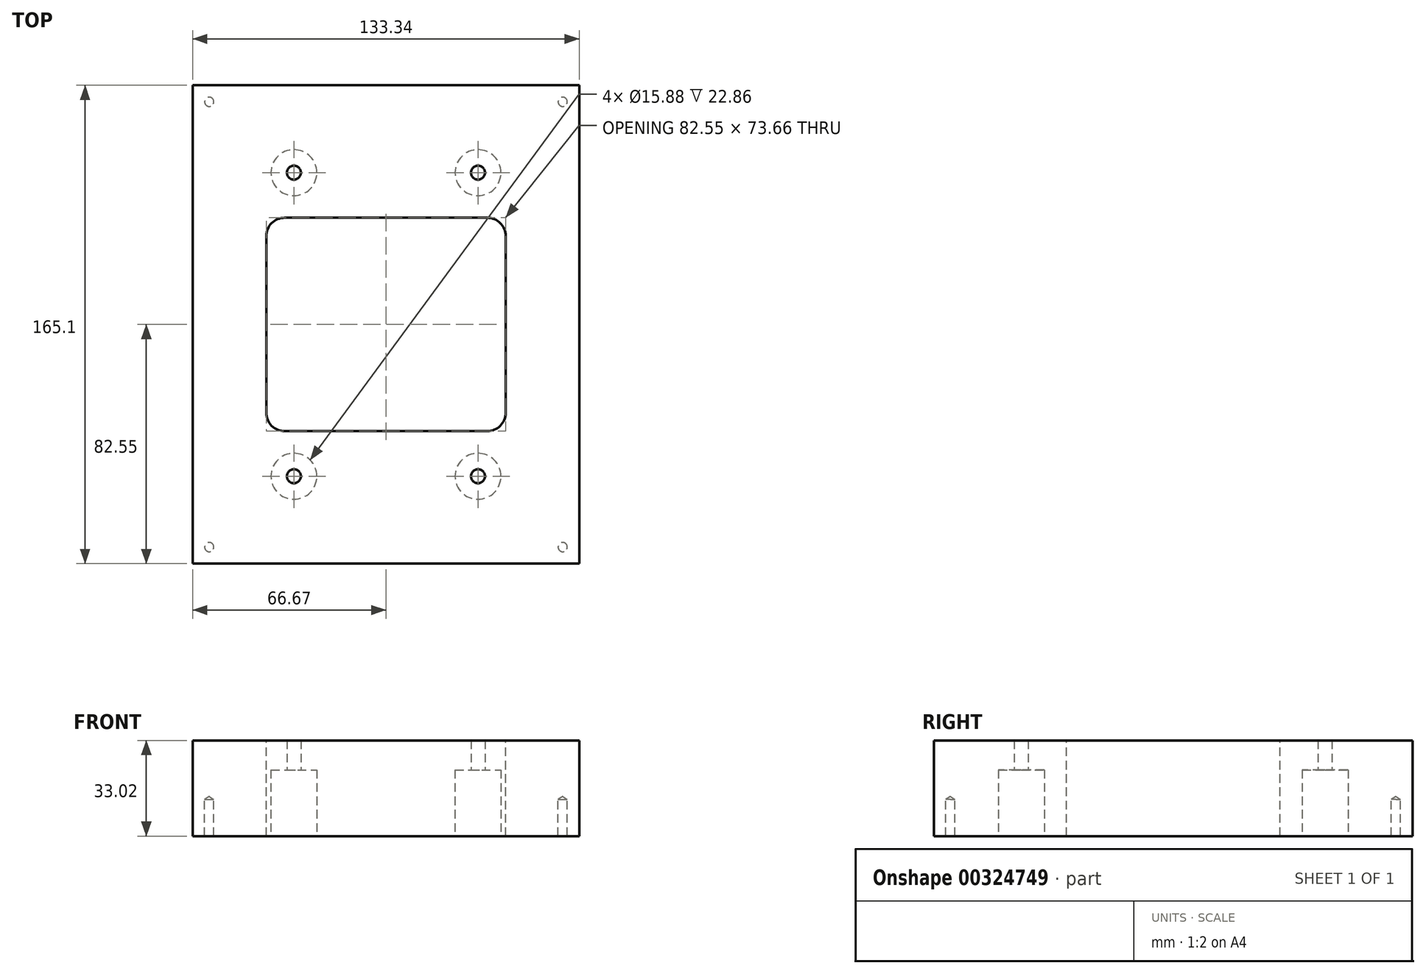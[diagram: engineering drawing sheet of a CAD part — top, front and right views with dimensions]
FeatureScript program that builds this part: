
annotation { "Feature Type Name" : "Feature", "Feature Type Description" : "" }
export const myFeature = defineFeature(function(context is Context, id is Id, definition is map)
    precondition{}
    {
        {
            var Q0;
            Q0=qCreatedBy(makeId("Top.planeOp"),FACE);
            var sketch = newSketch(context, id + "F0", { "sketchPlane" : qUnion([Q0])});
            skLineSegment(sketch, "E0.bottom", {"start": v(66.68, -82.55) * mm, "end": v(-66.68, -82.55) * mm});
            skLineSegment(sketch, "E0.top", {"start": v(66.68, 82.55) * mm, "end": v(-66.67, 82.55) * mm});
            skLineSegment(sketch, "E0.left", {"start": v(66.68, -82.55) * mm, "end": v(66.68, 82.55) * mm});
            skLineSegment(sketch, "E0.right", {"start": v(-66.68, -82.55) * mm, "end": v(-66.67, 82.55) * mm});
            skPoint(sketch, "E0.middle", {"position": v(0, 0) * mm});
            skSolve(sketch);
        }
        {
            var Q0;
            Q0 = qSketchRegion(id + "F0", true);
            extrude(context, id + "F1", {"entities" : qUnion([Q0]), "depth" : 33.02 * mm, "offsetDistance" : 25.4 * mm});
        }
        {
            var Q0;
            Q0=makeQuery(id+"F1.opExtrude","CAP_FACE",FACE,{"disambiguationData":[OSD([sQuery(id+"F0.wireOp",EDGE,"E0.bottom"),sQuery(id+"F0.wireOp",EDGE,"E0.top"),sQuery(id+"F0.wireOp",EDGE,"E0.left"),sQuery(id+"F0.wireOp",EDGE,"E0.right")])],"isStart":false});
            var sketch = newSketch(context, id + "F2", { "sketchPlane" : qUnion([Q0])});
            skLineSegment(sketch, "E1.bottom", {"start": v(-41.28, 36.83) * mm, "end": v(41.28, 36.83) * mm});
            skLineSegment(sketch, "E1.top", {"start": v(-41.28, -36.83) * mm, "end": v(41.28, -36.83) * mm});
            skLineSegment(sketch, "E1.left", {"start": v(-41.28, 36.83) * mm, "end": v(-41.28, -36.83) * mm});
            skLineSegment(sketch, "E1.right", {"start": v(41.28, 36.83) * mm, "end": v(41.28, -36.83) * mm});
            skSolve(sketch);
        }
        {
            var Q0;
            Q0=makeQuery(id+"F2.imprint","IMPRINT",FACE,{"disambiguationData":[TD([[makeQuery(id+"F2.imprint","IMPRINT",EDGE,{"derivedFrom":sQuery(id+"F2.wireOp",EDGE,"E1.bottom")}),-1.0]])]});
            extrude(context, id + "F3", {"entities" : qUnion([Q0]), "operationType" : NewBodyOperationType.REMOVE, "endBound" : BoundingType.THROUGH_ALL, "oppositeDirection" : true, "depth" : 25.4 * mm, "offsetDistance" : 25.4 * mm});
        }
        {
            var Q0;
            Q0=makeQuery(id+"F3.boolean.opBoolean","COPY",EDGE,{"derivedFrom":makeQuery(id+"F3.opExtrude","SWEPT_EDGE",EDGE,{"disambiguationData":[OSD([sQuery(id+"F2.wireOp",EDGE,"E1.bottom"),sQuery(id+"F2.wireOp",EDGE,"E1.left")])]})});
            var Q1;
            Q1=makeQuery(id+"F3.boolean.opBoolean","COPY",EDGE,{"derivedFrom":makeQuery(id+"F3.opExtrude","SWEPT_EDGE",EDGE,{"disambiguationData":[OSD([sQuery(id+"F2.wireOp",EDGE,"E1.top"),sQuery(id+"F2.wireOp",EDGE,"E1.left")])]})});
            var Q2;
            Q2=makeQuery(id+"F3.boolean.opBoolean","COPY",EDGE,{"derivedFrom":makeQuery(id+"F3.opExtrude","SWEPT_EDGE",EDGE,{"disambiguationData":[OSD([sQuery(id+"F2.wireOp",EDGE,"E1.top"),sQuery(id+"F2.wireOp",EDGE,"E1.right")])]})});
            var Q3;
            Q3=makeQuery(id+"F3.boolean.opBoolean","COPY",EDGE,{"derivedFrom":makeQuery(id+"F3.opExtrude","SWEPT_EDGE",EDGE,{"disambiguationData":[OSD([sQuery(id+"F2.wireOp",EDGE,"E1.bottom"),sQuery(id+"F2.wireOp",EDGE,"E1.right")])]})});
            fillet(context, id + "F4", {"entities" : qUnion([Q0, Q1, Q2, Q3]), "tangentPropagation" : true, "radius" : 6.35 * mm, "defaultsChanged" : false, "vertexSettings" : [], "allowEdgeOverflow" : false});
        }
        {
            var Q0;
            Q0=makeQuery(id+"F1.opExtrude","CAP_FACE",FACE,{"disambiguationData":[OSD([sQuery(id+"F0.wireOp",EDGE,"E0.bottom"),sQuery(id+"F0.wireOp",EDGE,"E0.top"),sQuery(id+"F0.wireOp",EDGE,"E0.left"),sQuery(id+"F0.wireOp",EDGE,"E0.right")])],"isStart":false});
            var sketch = newSketch(context, id + "F5", { "sketchPlane" : qUnion([Q0])});
            skPoint(sketch, "E2", {"position": v(-31.75, -52.39) * mm});
            skPoint(sketch, "E3", {"position": v(31.75, -52.39) * mm});
            skPoint(sketch, "E4", {"position": v(31.75, 52.39) * mm});
            skPoint(sketch, "E5", {"position": v(-31.75, 52.39) * mm});
            skSolve(sketch);
        }
        {
            var Q0;
            Q0=sQuery(id+"F5.wireOp",VERTEX,"E5");
            var Q1;
            Q1=sQuery(id+"F5.wireOp",VERTEX,"E4");
            var Q2;
            Q2=sQuery(id+"F5.wireOp",VERTEX,"E3");
            var Q3;
            Q3=sQuery(id+"F5.wireOp",VERTEX,"E2");
            var Q4;
            Q4=makeQuery(id+"F1.opExtrude","SWEPT_BODY",BODY,{"disambiguationData":[OSD([sQuery(id+"F0.wireOp",EDGE,"E0.bottom"),sQuery(id+"F0.wireOp",EDGE,"E0.top"),sQuery(id+"F0.wireOp",EDGE,"E0.left"),sQuery(id+"F0.wireOp",EDGE,"E0.right")])]});
            hole(context, id + "F6", {"style" : HoleStyle.SIMPLE, "endStyle" : HoleEndStyle.THROUGH, "holeDiameter" : 4.83 * mm, "majorDiameter" : 6.35 * mm, "tappedDepth" : 12.7 * mm, "tapClearance" : 3, "locations" : qUnion([Q0, Q1, Q2, Q3]), "scope" : qUnion([Q4])});
        }
        {
            var Q0;
            Q0=makeQuery(id+"F1.opExtrude","CAP_FACE",FACE,{"disambiguationData":[OSD([sQuery(id+"F0.wireOp",EDGE,"E0.bottom"),sQuery(id+"F0.wireOp",EDGE,"E0.top"),sQuery(id+"F0.wireOp",EDGE,"E0.left"),sQuery(id+"F0.wireOp",EDGE,"E0.right")])],"isStart":true});
            var sketch = newSketch(context, id + "F7", { "sketchPlane" : qUnion([Q0])});
            skCircle(sketch, "E6", {"center": v(-31.75, 52.39) * mm, "radius": 7.94 * mm});
            skCircle(sketch, "E7", {"center": v(31.75, 52.39) * mm, "radius": 7.94 * mm});
            skCircle(sketch, "E8", {"center": v(-31.75, -52.39) * mm, "radius": 7.94 * mm});
            skCircle(sketch, "E9", {"center": v(31.75, -52.39) * mm, "radius": 7.94 * mm});
            skSolve(sketch);
        }
        {
            var Q0;
            Q0=makeQuery(id+"F7.imprint","IMPRINT",FACE,{"disambiguationData":[TD([[makeQuery(id+"F7.imprint","IMPRINT",EDGE,{"derivedFrom":sQuery(id+"F7.wireOp",EDGE,"E6")}),1.0]])]});
            var Q1;
            Q1=makeQuery(id+"F7.imprint","IMPRINT",FACE,{"disambiguationData":[TD([[makeQuery(id+"F7.imprint","IMPRINT",EDGE,{"derivedFrom":sQuery(id+"F7.wireOp",EDGE,"E7")}),1.0]])]});
            var Q2;
            Q2=makeQuery(id+"F7.imprint","IMPRINT",FACE,{"disambiguationData":[TD([[makeQuery(id+"F7.imprint","IMPRINT",EDGE,{"derivedFrom":sQuery(id+"F7.wireOp",EDGE,"E9")}),1.0]])]});
            var Q3;
            Q3=makeQuery(id+"F7.imprint","IMPRINT",FACE,{"disambiguationData":[TD([[makeQuery(id+"F7.imprint","IMPRINT",EDGE,{"derivedFrom":sQuery(id+"F7.wireOp",EDGE,"E8")}),1.0]])]});
            extrude(context, id + "F8", {"entities" : qUnion([Q0, Q1, Q2, Q3]), "operationType" : NewBodyOperationType.REMOVE, "oppositeDirection" : true, "depth" : 22.86 * mm, "offsetDistance" : 25.4 * mm});
        }
        {
            var Q0;
            Q0=makeQuery(id+"F1.opExtrude","CAP_FACE",FACE,{"disambiguationData":[OSD([sQuery(id+"F0.wireOp",EDGE,"E0.bottom"),sQuery(id+"F0.wireOp",EDGE,"E0.top"),sQuery(id+"F0.wireOp",EDGE,"E0.left"),sQuery(id+"F0.wireOp",EDGE,"E0.right")])],"isStart":true});
            var sketch = newSketch(context, id + "F9", { "sketchPlane" : qUnion([Q0])});
            skPoint(sketch, "E10", {"position": v(-60.96, 76.84) * mm});
            skPoint(sketch, "E11", {"position": v(60.96, 76.84) * mm});
            skPoint(sketch, "E12", {"position": v(60.96, -76.83) * mm});
            skPoint(sketch, "E13", {"position": v(-60.96, -76.83) * mm});
            skSolve(sketch);
        }
        {
            var Q0;
            Q0=sQuery(id+"F9.wireOp",VERTEX,"E10");
            var Q1;
            Q1=sQuery(id+"F9.wireOp",VERTEX,"E11");
            var Q2;
            Q2=sQuery(id+"F9.wireOp",VERTEX,"E12");
            var Q3;
            Q3=sQuery(id+"F9.wireOp",VERTEX,"E13");
            var Q4;
            Q4=makeQuery(id+"F1.opExtrude","SWEPT_BODY",BODY,{"disambiguationData":[OSD([sQuery(id+"F0.wireOp",EDGE,"E0.bottom"),sQuery(id+"F0.wireOp",EDGE,"E0.top"),sQuery(id+"F0.wireOp",EDGE,"E0.left"),sQuery(id+"F0.wireOp",EDGE,"E0.right")])]});
            hole(context, id + "F10", {"style" : HoleStyle.SIMPLE, "endStyle" : HoleEndStyle.BLIND, "holeDiameter" : 3.17 * mm, "majorDiameter" : 6.35 * mm, "holeDepth" : 12.7 * mm, "tappedDepth" : 12.7 * mm, "tapClearance" : 3, "locations" : qUnion([Q0, Q1, Q2, Q3]), "scope" : qUnion([Q4])});
        }
    });
